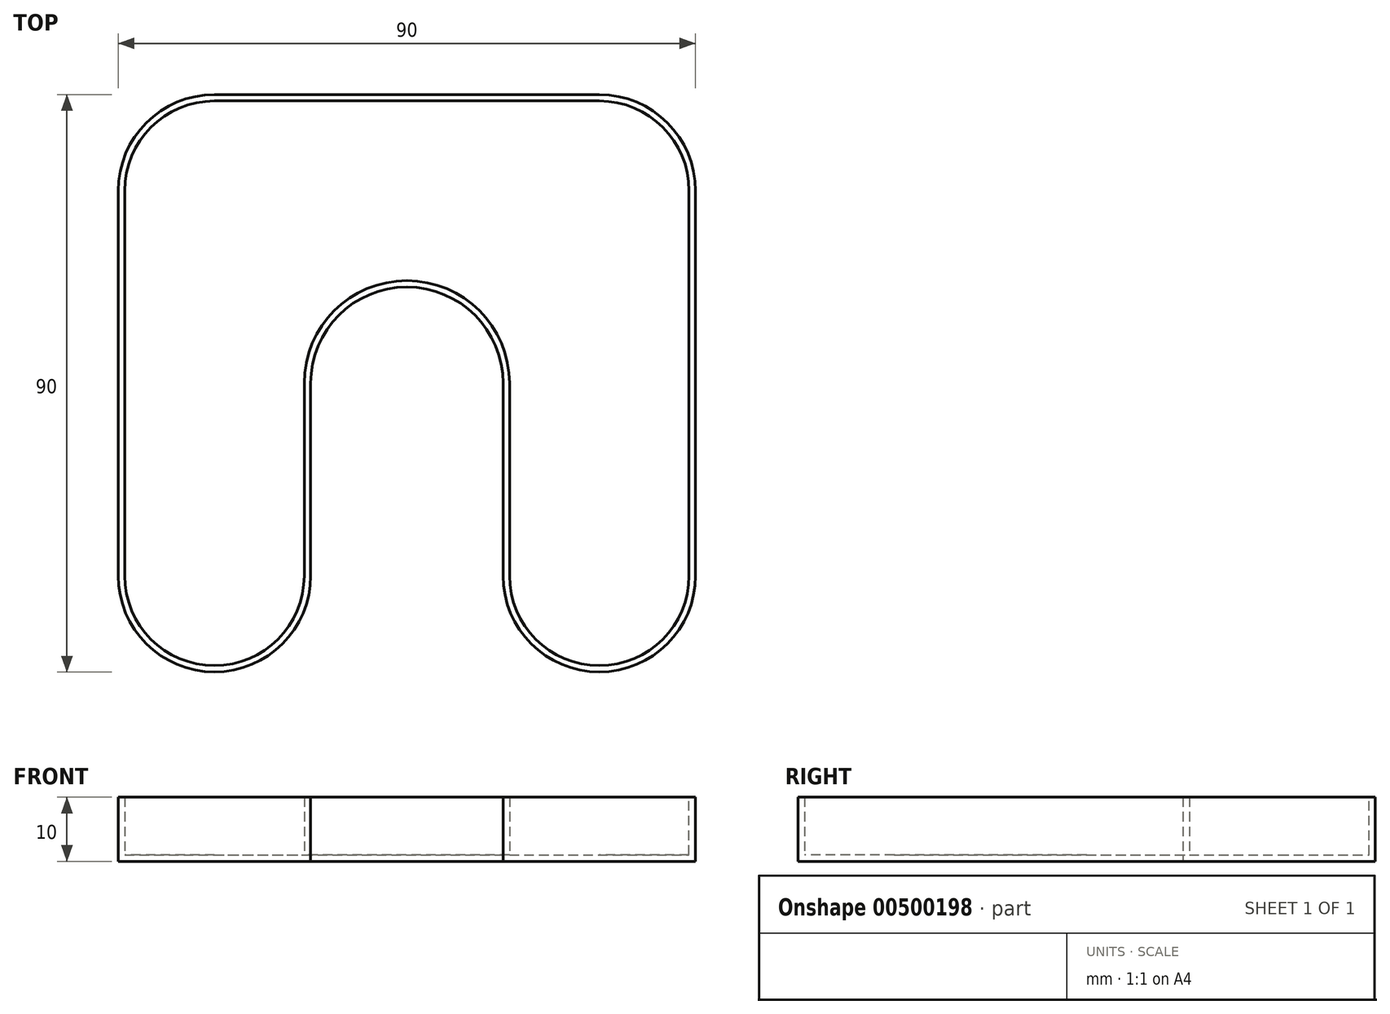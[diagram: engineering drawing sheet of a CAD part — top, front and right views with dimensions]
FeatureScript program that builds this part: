
annotation { "Feature Type Name" : "Feature", "Feature Type Description" : "" }
export const myFeature = defineFeature(function(context is Context, id is Id, definition is map)
    precondition{}
    {
        {
            var Q0;
            Q0=qCreatedBy(makeId("Top.planeOp"),FACE);
            var sketch = newSketch(context, id + "F0", { "sketchPlane" : qUnion([Q0])});
            skLineSegment(sketch, "E0.bottom", {"start": v(8.02, 0) * mm, "end": v(8.02, 0) * mm});
            skLineSegment(sketch, "E0.top", {"start": v(8.02, 90) * mm, "end": v(68.02, 90) * mm});
            skLineSegment(sketch, "E0.left", {"start": v(-6.98, 15) * mm, "end": v(-6.98, 75) * mm});
            skLineSegment(sketch, "E0.right", {"start": v(83.02, 15) * mm, "end": v(83.02, 75) * mm});
            skLineSegment(sketch, "E1", {"start": v(23.02, 17.93) * mm, "end": v(23.02, 15) * mm});
            skLineSegment(sketch, "E2", {"start": v(53.02, 17.93) * mm, "end": v(53.02, 15) * mm});
            skLineSegment(sketch, "E3.trimOffspring", {"start": v(38.02, 32.93) * mm, "end": v(38.02, 32.93) * mm});
            skLineSegment(sketch, "E4.trimOffspring", {"start": v(68.02, 0) * mm, "end": v(68.02, 0) * mm});
            skPoint(sketch, "E5.visualSharp", {"position": v(-6.98, 90) * mm});
            skArc(sketch, "E5.filletArc", {"start": v(8.02, 90) * mm, "mid": v(-2.58, 85.6) * mm, "end": v(-6.98, 75) * mm});
            skPoint(sketch, "E6.visualSharp", {"position": v(83.02, 90) * mm});
            skArc(sketch, "E6.filletArc", {"start": v(83.02, 75) * mm, "mid": v(78.63, 85.6) * mm, "end": v(68.02, 90) * mm});
            skPoint(sketch, "E7.visualSharp", {"position": v(-6.98, 0) * mm});
            skArc(sketch, "E7.filletArc", {"start": v(-6.98, 15) * mm, "mid": v(-2.58, 4.4) * mm, "end": v(8.02, 0) * mm});
            skPoint(sketch, "E8.visualSharp", {"position": v(23.02, 0) * mm});
            skArc(sketch, "E8.filletArc", {"start": v(8.02, 0) * mm, "mid": v(18.63, 4.4) * mm, "end": v(23.02, 15) * mm});
            skPoint(sketch, "E9.visualSharp", {"position": v(53.02, 0) * mm});
            skArc(sketch, "E9.filletArc", {"start": v(53.02, 15) * mm, "mid": v(57.42, 4.4) * mm, "end": v(68.02, 0) * mm});
            skPoint(sketch, "E10.visualSharp", {"position": v(83.02, 0) * mm});
            skArc(sketch, "E10.filletArc", {"start": v(68.02, 0) * mm, "mid": v(78.63, 4.4) * mm, "end": v(83.02, 15) * mm});
            skPoint(sketch, "E11.visualSharp", {"position": v(23.02, 32.93) * mm});
            skPoint(sketch, "E12.visualSharp", {"position": v(53.02, 32.93) * mm});
            skLineSegment(sketch, "E13", {"start": v(23.02, 0) * mm, "end": v(23.02, 45) * mm});
            skLineSegment(sketch, "E14", {"start": v(38.02, 60) * mm, "end": v(38.02, 60) * mm});
            skLineSegment(sketch, "E15", {"start": v(53.02, 45) * mm, "end": v(53.02, 17.93) * mm});
            skPoint(sketch, "E16.visualSharp", {"position": v(23.02, 60) * mm});
            skArc(sketch, "E16.filletArc", {"start": v(38.02, 60) * mm, "mid": v(27.42, 55.6) * mm, "end": v(23.02, 45) * mm});
            skPoint(sketch, "E17.visualSharp", {"position": v(53.02, 60) * mm});
            skArc(sketch, "E17.filletArc", {"start": v(53.02, 45) * mm, "mid": v(48.63, 55.6) * mm, "end": v(38.02, 60) * mm});
            skSolve(sketch);
        }
        {
            var Q0;
            Q0=makeQuery(id+"F0.imprint","IMPRINT",FACE,{"disambiguationData":[TD([[makeQuery(id+"F0.imprint","IMPRINT",EDGE,{"derivedFrom":sQuery(id+"F0.wireOp",EDGE,"E0.top")}),-1.0]])]});
            extrude(context, id + "F1", {"entities" : qUnion([Q0]), "depth" : 10 * mm});
        }
        {
            var Q0;
            Q0=makeQuery(id+"F1.opExtrude","CAP_FACE",FACE,{"disambiguationData":[OSD([sQuery(id+"F0.wireOp",EDGE,"E0.top"),sQuery(id+"F0.wireOp",EDGE,"E0.left"),sQuery(id+"F0.wireOp",EDGE,"E0.right"),sQuery(id+"F0.wireOp",EDGE,"E2"),sQuery(id+"F0.wireOp",EDGE,"E5.filletArc"),sQuery(id+"F0.wireOp",EDGE,"E6.filletArc"),sQuery(id+"F0.wireOp",EDGE,"E7.filletArc"),sQuery(id+"F0.wireOp",EDGE,"E8.filletArc"),sQuery(id+"F0.wireOp",EDGE,"E9.filletArc"),sQuery(id+"F0.wireOp",EDGE,"E10.filletArc"),sQuery(id+"F0.wireOp",EDGE,"E13"),sQuery(id+"F0.wireOp",EDGE,"E15"),sQuery(id+"F0.wireOp",EDGE,"E16.filletArc"),sQuery(id+"F0.wireOp",EDGE,"E17.filletArc")])],"isStart":false});
            shell(context, id + "F2", {"entities" : qUnion([Q0]), "thickness" : 1 * mm});
        }
    });
